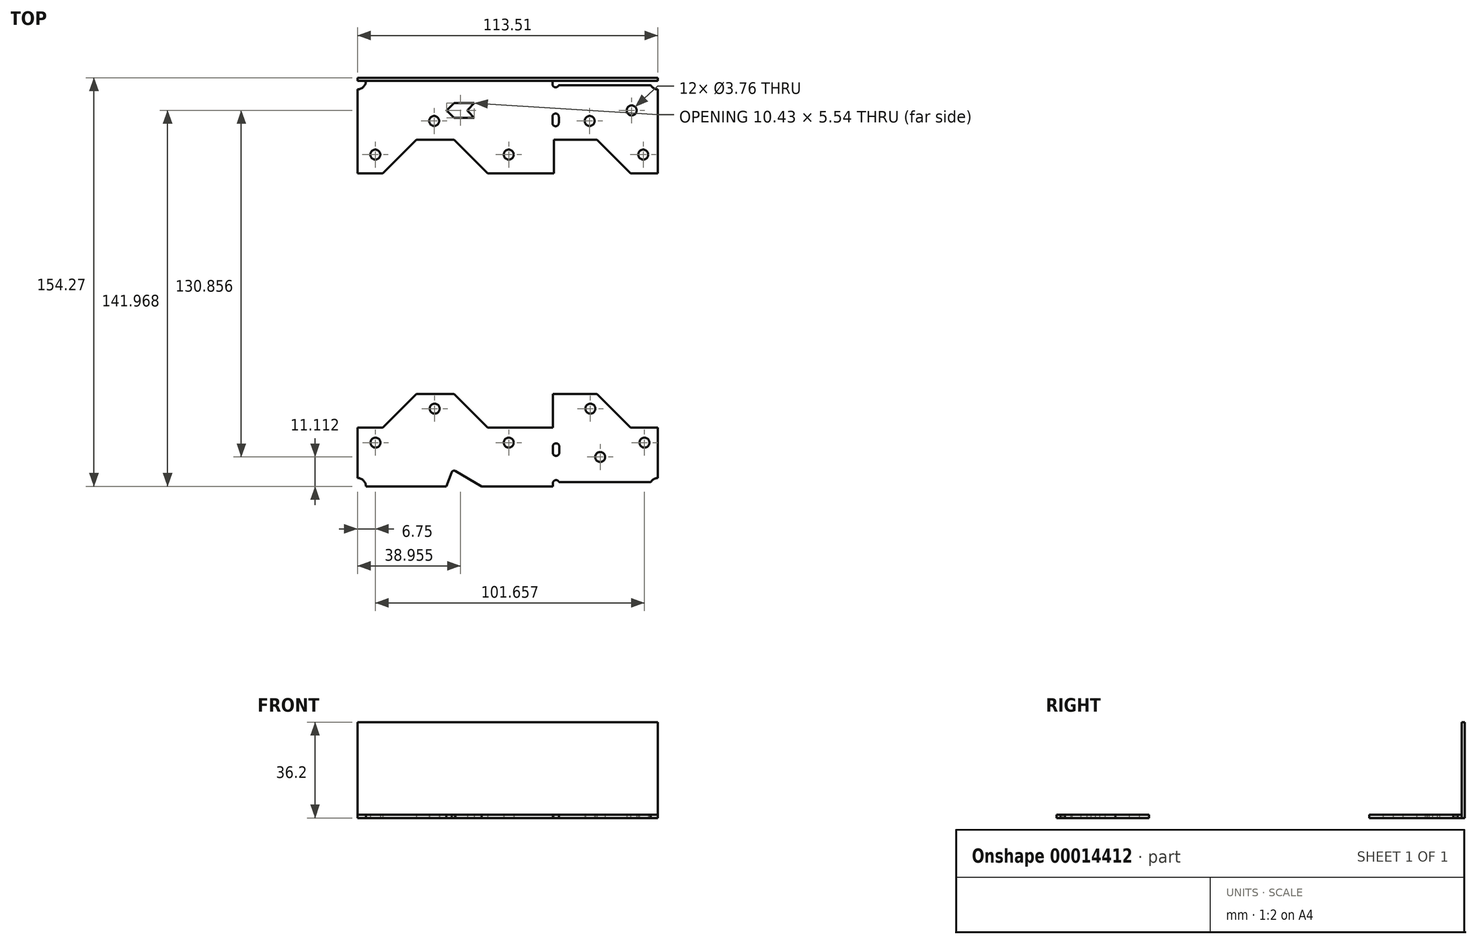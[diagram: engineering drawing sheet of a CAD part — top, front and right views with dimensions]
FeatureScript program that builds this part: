
annotation { "Feature Type Name" : "Feature", "Feature Type Description" : "" }
export const myFeature = defineFeature(function(context is Context, id is Id, definition is map)
    precondition{}
    {
        {
            var Q0;
            Q0=qCreatedBy(makeId("Top.planeOp"),FACE);
            var sketch = newSketch(context, id + "F0", { "sketchPlane" : qUnion([Q0])});
            skArc(sketch, "E0", {"start": v(-106.43, 73.37) * mm, "mid": v(-104.18, 74.3) * mm, "end": v(-103.25, 76.54) * mm});
            skArc(sketch, "E1", {"start": v(4.33, 74.95) * mm, "mid": v(5.5, 73.8) * mm, "end": v(7.08, 73.37) * mm});
            skLineSegment(sketch, "E2", {"start": v(-106.43, 73.38) * mm, "end": v(-106.43, 41.62) * mm});
            skLineSegment(sketch, "E3", {"start": v(-32.76, 60.68) * mm, "end": v(-32.76, 63.05) * mm});
            skLineSegment(sketch, "E4", {"start": v(-30.38, 63.05) * mm, "end": v(-30.38, 60.68) * mm});
            skArc(sketch, "E5", {"start": v(-32.76, 60.68) * mm, "mid": v(-31.57, 59.48) * mm, "end": v(-30.38, 60.68) * mm});
            skArc(sketch, "E6", {"start": v(-30.38, 63.05) * mm, "mid": v(-31.57, 64.25) * mm, "end": v(-32.76, 63.05) * mm});
            skLineSegment(sketch, "E7", {"start": v(-106.43, 41.62) * mm, "end": v(-96.9, 41.62) * mm});
            skLineSegment(sketch, "E8", {"start": v(-96.9, 41.62) * mm, "end": v(-96.9, 41.62) * mm});
            skLineSegment(sketch, "E9", {"start": v(-32.21, 41.62) * mm, "end": v(-32.21, 54.32) * mm});
            skLineSegment(sketch, "E10", {"start": v(-32.21, 54.32) * mm, "end": v(-15.94, 54.32) * mm});
            skLineSegment(sketch, "E11", {"start": v(-15.94, 54.32) * mm, "end": v(-15.94, 54.32) * mm});
            skLineSegment(sketch, "E12", {"start": v(-3.24, 41.62) * mm, "end": v(7.08, 41.62) * mm});
            skLineSegment(sketch, "E13", {"start": v(7.08, 41.62) * mm, "end": v(7.08, 73.37) * mm});
            skLineSegment(sketch, "E14", {"start": v(4.26, 74.95) * mm, "end": v(-30.45, 74.95) * mm});
            skLineSegment(sketch, "E15", {"start": v(-15.94, 54.32) * mm, "end": v(-3.24, 41.62) * mm});
            skLineSegment(sketch, "E16", {"start": v(-84.2, 54.32) * mm, "end": v(-96.9, 41.62) * mm});
            skCircle(sketch, "E17", {"center": v(-99.68, 48.76) * mm, "radius": 1.88 * mm});
            skCircle(sketch, "E18", {"center": v(-49.28, 48.76) * mm, "radius": 1.88 * mm});
            skCircle(sketch, "E19", {"center": v(1.52, 48.76) * mm, "radius": 1.88 * mm});
            skCircle(sketch, "E20", {"center": v(-77.45, 61.46) * mm, "radius": 1.88 * mm});
            skCircle(sketch, "E21", {"center": v(-18.72, 61.46) * mm, "radius": 1.88 * mm});
            skCircle(sketch, "E22", {"center": v(-2.84, 65.43) * mm, "radius": 1.88 * mm});
            skLineSegment(sketch, "E23", {"start": v(-32.76, 75.35) * mm, "end": v(-32.76, 76.54) * mm});
            skArc(sketch, "E24", {"start": v(-32.76, 75.35) * mm, "mid": v(-31.77, 74.18) * mm, "end": v(-30.45, 74.95) * mm});
            skLineSegment(sketch, "E25", {"start": v(-57.21, 41.62) * mm, "end": v(-32.21, 41.62) * mm});
            skLineSegment(sketch, "E26", {"start": v(-57.21, 41.62) * mm, "end": v(-69.91, 54.32) * mm});
            skLineSegment(sketch, "E27", {"start": v(-84.2, 54.32) * mm, "end": v(-69.91, 54.32) * mm});
            skLineSegment(sketch, "E28", {"start": v(-106.43, 77.73) * mm, "end": v(-106.43, 76.54) * mm});
            skLineSegment(sketch, "E29", {"start": v(7.08, 76.54) * mm, "end": v(-106.43, 76.54) * mm});
            skLineSegment(sketch, "E30", {"start": v(7.08, 77.73) * mm, "end": v(-106.43, 77.73) * mm});
            skLineSegment(sketch, "E31", {"start": v(7.08, 76.54) * mm, "end": v(7.08, 77.73) * mm});
            skLineSegment(sketch, "E32", {"start": v(-69.92, 62.66) * mm, "end": v(-47.3, 62.66) * mm});
            skLineSegment(sketch, "E33", {"start": v(-69.92, 68.2) * mm, "end": v(-47.3, 68.2) * mm});
            skArc(sketch, "E34", {"start": v(-64.75, 65.7) * mm, "mid": v(-64.87, 65.42) * mm, "end": v(-64.75, 65.14) * mm});
            skLineSegment(sketch, "E35", {"start": v(-64.75, 65.14) * mm, "end": v(-62.27, 62.66) * mm});
            skLineSegment(sketch, "E36", {"start": v(-64.75, 65.7) * mm, "end": v(-62.26, 68.2) * mm});
            skLineSegment(sketch, "E37", {"start": v(-72.7, 65.43) * mm, "end": v(-69.92, 62.66) * mm});
            skLineSegment(sketch, "E38", {"start": v(-72.7, 65.43) * mm, "end": v(-69.92, 68.2) * mm});
            skArc(sketch, "E39", {"start": v(-103.25, -76.54) * mm, "mid": v(-104.18, -74.3) * mm, "end": v(-106.43, -73.37) * mm});
            skArc(sketch, "E40", {"start": v(7.08, -73.37) * mm, "mid": v(5.5, -73.8) * mm, "end": v(4.33, -74.95) * mm});
            skLineSegment(sketch, "E41", {"start": v(-30.22, -61.46) * mm, "end": v(-30.22, -63.83) * mm});
            skLineSegment(sketch, "E42", {"start": v(-32.61, -63.83) * mm, "end": v(-32.61, -61.46) * mm});
            skArc(sketch, "E43", {"start": v(-30.22, -61.46) * mm, "mid": v(-31.42, -60.27) * mm, "end": v(-32.61, -61.46) * mm});
            skArc(sketch, "E44", {"start": v(-32.61, -63.83) * mm, "mid": v(-31.42, -65.03) * mm, "end": v(-30.22, -63.83) * mm});
            skLineSegment(sketch, "E45", {"start": v(-15.94, -41.62) * mm, "end": v(-3.24, -54.32) * mm});
            skLineSegment(sketch, "E46", {"start": v(-32.6, -54.32) * mm, "end": v(-32.6, -41.62) * mm});
            skLineSegment(sketch, "E47", {"start": v(-106.43, -54.32) * mm, "end": v(-96.9, -54.32) * mm});
            skCircle(sketch, "E48", {"center": v(-99.62, -60.02) * mm, "radius": 1.88 * mm});
            skCircle(sketch, "E49", {"center": v(-49.28, -60.02) * mm, "radius": 1.88 * mm});
            skCircle(sketch, "E50", {"center": v(1.98, -60.02) * mm, "radius": 1.88 * mm});
            skCircle(sketch, "E51", {"center": v(-77.27, -47.2) * mm, "radius": 1.88 * mm});
            skCircle(sketch, "E52", {"center": v(-18.45, -47.2) * mm, "radius": 1.88 * mm});
            skCircle(sketch, "E53", {"center": v(-14.75, -65.43) * mm, "radius": 1.88 * mm});
            skArc(sketch, "E54", {"start": v(-30.3, -74.95) * mm, "mid": v(-31.62, -74.18) * mm, "end": v(-32.61, -75.35) * mm});
            skLineSegment(sketch, "E55", {"start": v(-57.21, -54.32) * mm, "end": v(-69.91, -41.62) * mm});
            skLineSegment(sketch, "E56", {"start": v(-106.43, -76.54) * mm, "end": v(7.08, -76.54) * mm});
            skLineSegment(sketch, "E57", {"start": v(-106.43, -77.73) * mm, "end": v(7.08, -77.73) * mm});
            skArc(sketch, "E58", {"start": v(-68.88, -69.64) * mm, "mid": v(-70.56, -69.48) * mm, "end": v(-71.88, -70.53) * mm});
            skArc(sketch, "E59", {"start": v(-69.37, -70.73) * mm, "mid": v(-70.21, -70.65) * mm, "end": v(-70.87, -71.17) * mm});
            skLineSegment(sketch, "E60", {"start": v(-74.28, -76.54) * mm, "end": v(-71.88, -70.53) * mm});
            skLineSegment(sketch, "E61", {"start": v(-68.88, -69.64) * mm, "end": v(-56.63, -76.54) * mm});
            skLineSegment(sketch, "E62", {"start": v(-69.37, -70.73) * mm, "end": v(-59.47, -76.54) * mm});
            skLineSegment(sketch, "E63", {"start": v(-72.87, -76.54) * mm, "end": v(-70.87, -71.17) * mm});
            skLineSegment(sketch, "E64", {"start": v(105.24, -41.62) * mm, "end": v(106.43, -41.62) * mm});
            skLineSegment(sketch, "E65", {"start": v(71.5, -77.73) * mm, "end": v(103.78, -77.73) * mm});
            skLineSegment(sketch, "E66", {"start": v(106.43, -41.62) * mm, "end": v(106.43, -75.09) * mm});
            skLineSegment(sketch, "E67", {"start": v(71.5, -76.54) * mm, "end": v(71.5, -77.73) * mm});
            skLineSegment(sketch, "E68", {"start": v(105.24, -41.62) * mm, "end": v(105.24, -75.22) * mm});
            skLineSegment(sketch, "E69", {"start": v(71.5, -76.54) * mm, "end": v(103.92, -76.54) * mm});
            skArc(sketch, "E70", {"start": v(103.92, -76.54) * mm, "mid": v(104.85, -76.15) * mm, "end": v(105.24, -75.22) * mm});
            skArc(sketch, "E71", {"start": v(103.78, -77.73) * mm, "mid": v(105.65, -76.96) * mm, "end": v(106.43, -75.09) * mm});
            skLineSegment(sketch, "E72", {"start": v(97.3, -69.4) * mm, "end": v(97.3, -76.54) * mm});
            skLineSegment(sketch, "E73", {"start": v(91.75, -69.4) * mm, "end": v(91.75, -76.54) * mm});
            skLineSegment(sketch, "E74", {"start": v(91.75, -69.4) * mm, "end": v(97.3, -69.4) * mm});
            skLineSegment(sketch, "E75", {"start": v(-106.43, 73.38) * mm, "end": v(-106.41, 73.37) * mm});
            skLineSegment(sketch, "E76", {"start": v(4.26, 74.95) * mm, "end": v(4.33, 74.95) * mm});
            skLineSegment(sketch, "E77", {"start": v(-32.61, -61.46) * mm, "end": v(-32.61, -61.46) * mm});
            skPoint(sketch, "E78.start.orphan", {"position": v(-29.34, -63.83) * mm});
            skLineSegment(sketch, "E79", {"start": v(7.08, -73.37) * mm, "end": v(7.08, -54.32) * mm});
            skLineSegment(sketch, "E80", {"start": v(-3.24, -54.32) * mm, "end": v(7.08, -54.32) * mm});
            skLineSegment(sketch, "E81", {"start": v(-32.6, -41.62) * mm, "end": v(-15.94, -41.62) * mm});
            skLineSegment(sketch, "E82", {"start": v(-57.21, -54.32) * mm, "end": v(-32.6, -54.32) * mm});
            skLineSegment(sketch, "E83", {"start": v(-32.61, -75.35) * mm, "end": v(-32.61, -76.54) * mm});
            skLineSegment(sketch, "E84", {"start": v(-84.2, -41.62) * mm, "end": v(-69.91, -41.62) * mm});
            skLineSegment(sketch, "E85", {"start": v(-84.2, -41.62) * mm, "end": v(-96.9, -54.32) * mm});
            skLineSegment(sketch, "E86", {"start": v(-106.43, -54.32) * mm, "end": v(-106.43, -73.37) * mm});
            skLineSegment(sketch, "E87", {"start": v(-30.3, -74.95) * mm, "end": v(4.33, -74.95) * mm});
            skLineSegment(sketch, "E88", {"start": v(-106.43, -76.54) * mm, "end": v(-106.43, -77.73) * mm});
            skLineSegment(sketch, "E89", {"start": v(7.08, -76.54) * mm, "end": v(7.08, -77.73) * mm});
            skSolve(sketch);
        }
        {
            var Q0;
            {var subQ2=sQuery(id+"F0.wireOp",EDGE,"E28");Q0=makeQuery(id+"F0.imprint","IMPRINT",FACE,{"disambiguationData":[TD([[makeQuery(id+"F0.imprint","IMPRINT",EDGE,{"derivedFrom":subQ2}),1.0]])]});}
            extrude(context, id + "F1", {"entities" : qUnion([Q0]), "depth" : 36.2 * mm});
        }
        {
            var Q0;
            Q0=makeQuery(id+"F0.imprint","IMPRINT",FACE,{"disambiguationData":[TD([[makeQuery(id+"F0.imprint","IMPRINT",EDGE,{"derivedFrom":sQuery(id+"F0.wireOp",EDGE,"E1")}),-1.0]])]});
            extrude(context, id + "F2", {"entities" : qUnion([Q0]), "operationType" : NewBodyOperationType.ADD, "depth" : 1.27 * mm});
        }
        {
            var Q0;
            Q0=makeQuery(id+"F1.opExtrude","SWEPT_FACE",FACE,{"disambiguationData":[OSD([sQuery(id+"F0.wireOp",EDGE,"E30")])]});
            cPlane(context, id + "F3", {"entities" : qUnion([Q0]), "cplaneType" : CPlaneType.OFFSET, "offset" : 0 * mm, "width" : 152.4 * mm, "height" : 152.4 * mm});
        }
        {
            var Q0;
            Q0=makeQuery(id+"F0.imprint","IMPRINT",FACE,{"disambiguationData":[TD([[makeQuery(id+"F0.imprint","IMPRINT",EDGE,{"derivedFrom":sQuery(id+"F0.wireOp",EDGE,"E42")}),1.0]])]});
            var Q1;
            Q1=makeQuery(id+"F0.imprint","IMPRINT",FACE,{"disambiguationData":[TD([[makeQuery(id+"F0.imprint","IMPRINT",EDGE,{"derivedFrom":sQuery(id+"F0.wireOp",EDGE,"8ec8726a-d74b-4f34-a8d3-de22c13ca951")}),1.0]])]});
            var Q2;
            {var subQ1=sQuery(id+"F0.wireOp",EDGE,"E61");Q2=makeQuery(id+"F0.imprint","IMPRINT",FACE,{"disambiguationData":[TD([[makeQuery(id+"F0.imprint","IMPRINT",EDGE,{"derivedFrom":subQ1}),1.0]])]});}
            var Q3;
            Q3=makeQuery(id+"F0.imprint","IMPRINT",FACE,{"disambiguationData":[TD([[makeQuery(id+"F0.imprint","IMPRINT",EDGE,{"derivedFrom":sQuery(id+"F0.wireOp",EDGE,"E40")}),-1.0]])]});
            var Q4;
            Q4=makeQuery(id+"F0.imprint","IMPRINT",FACE,{"disambiguationData":[TD([[makeQuery(id+"F0.imprint","IMPRINT",EDGE,{"derivedFrom":sQuery(id+"F0.wireOp",EDGE,"E41")}),1.0]])]});
            var Q5;
            {var subQ2=sQuery(id+"F0.wireOp",EDGE,"E39");Q5=makeQuery(id+"F0.imprint","IMPRINT",FACE,{"disambiguationData":[TD([[makeQuery(id+"F0.imprint","IMPRINT",EDGE,{"derivedFrom":subQ2}),-1.0]])]});}
            var Q6;
            Q6=makeQuery(id+"F0.imprint","IMPRINT",FACE,{"disambiguationData":[TD([[makeQuery(id+"F0.imprint","IMPRINT",EDGE,{"derivedFrom":sQuery(id+"F0.wireOp",EDGE,"987ce22b-a0d1-450b-8565-18346b81547d")}),-1.0]])]});
            var Q7;
            Q7=makeQuery(id+"F0.imprint","IMPRINT",FACE,{"disambiguationData":[TD([[makeQuery(id+"F0.imprint","IMPRINT",EDGE,{"derivedFrom":sQuery(id+"F0.wireOp",EDGE,"E58")}),1.0]])]});
            extrude(context, id + "F4", {"entities" : qUnion([Q0, Q1, Q2, Q3, Q4, Q5, Q6, Q7]), "depth" : 1.27 * mm});
        }
    });
